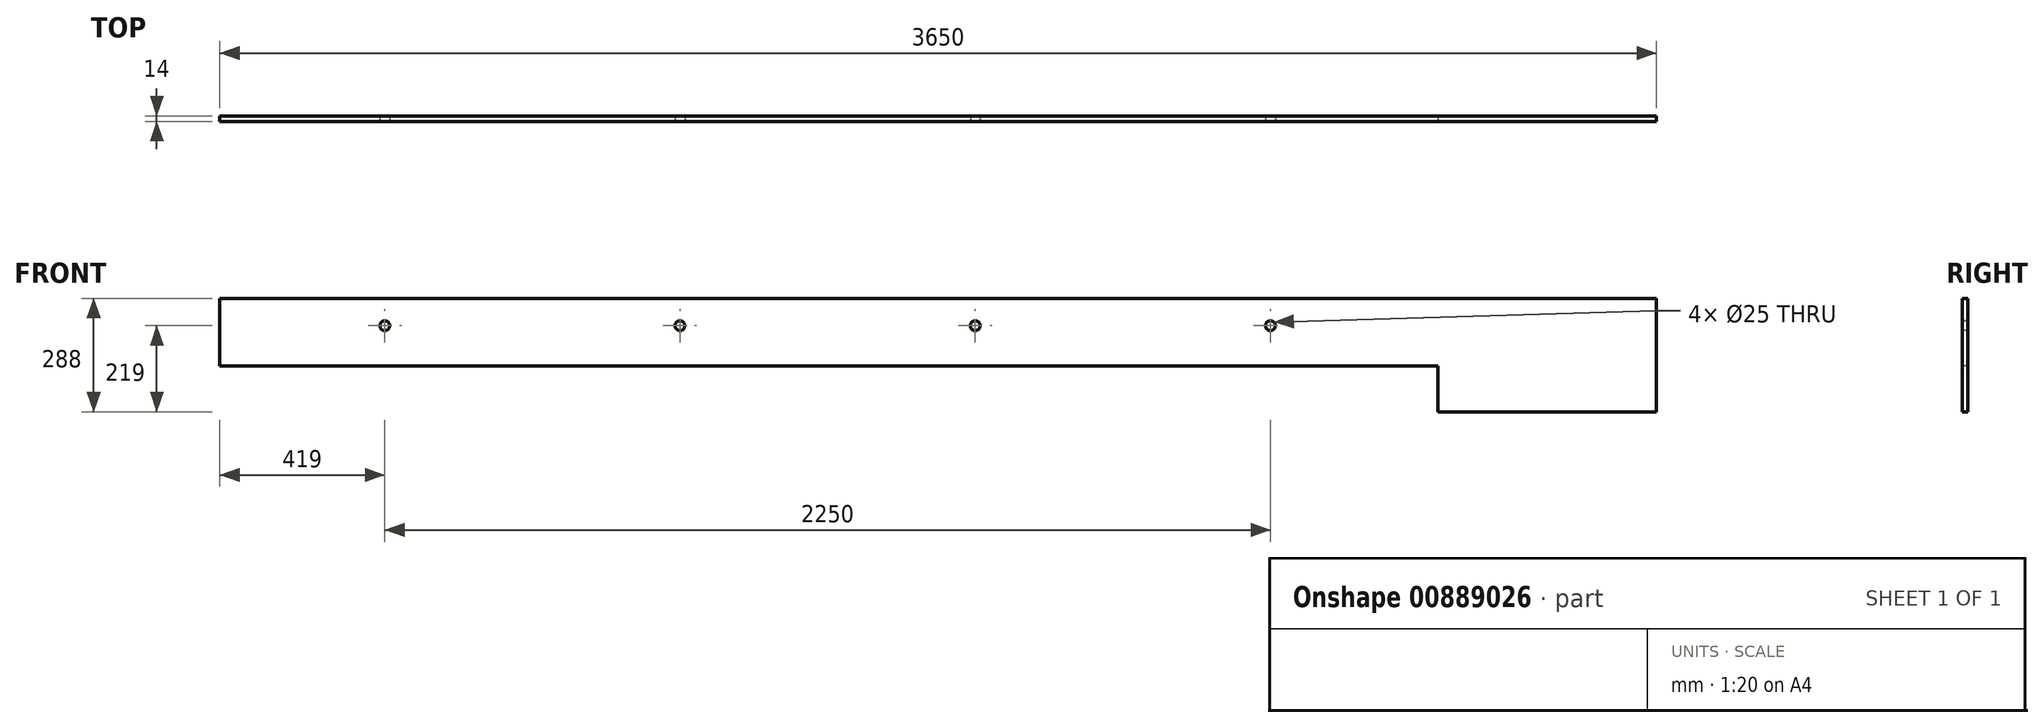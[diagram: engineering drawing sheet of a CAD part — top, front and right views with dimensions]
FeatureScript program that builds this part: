
annotation { "Feature Type Name" : "Feature", "Feature Type Description" : "" }
export const myFeature = defineFeature(function(context is Context, id is Id, definition is map)
    precondition{}
    {
        {
            var Q0;
            Q0=qCreatedBy(makeId("Right.planeOp"),FACE);
            var sketch = newSketch(context, id + "F0", { "sketchPlane" : qUnion([Q0])});
            skLineSegment(sketch, "E0.bottom", {"start": v(-7, 144) * mm, "end": v(7, 144) * mm});
            skLineSegment(sketch, "E0.top", {"start": v(-7, -144) * mm, "end": v(7, -144) * mm});
            skLineSegment(sketch, "E0.left", {"start": v(-7, 144) * mm, "end": v(-7, -144) * mm});
            skLineSegment(sketch, "E0.right", {"start": v(7, 144) * mm, "end": v(7, -144) * mm});
            skPoint(sketch, "E0.middle", {"position": v(0, 0) * mm});
            skSolve(sketch);
        }
        {
            var Q0;
            Q0 = qSketchRegion(id + "F0", true);
            extrude(context, id + "F1", {"entities" : qUnion([Q0]), "endBound" : BoundingType.SYMMETRIC, "depth" : 3650 * mm, "offsetDistance" : 25 * mm});
        }
        {
            var Q0;
            Q0=makeQuery(id+"F1.opExtrude","SWEPT_FACE",FACE,{"disambiguationData":[OSD([sQuery(id+"F0.wireOp",EDGE,"E0.left")])]});
            var sketch = newSketch(context, id + "F2", { "sketchPlane" : qUnion([Q0])});
            skLineSegment(sketch, "E1.bottom", {"start": v(-1825, -144) * mm, "end": v(1270, -144) * mm});
            skLineSegment(sketch, "E1.top", {"start": v(-1825, -27) * mm, "end": v(1270, -27) * mm});
            skLineSegment(sketch, "E1.left", {"start": v(-1825, -144) * mm, "end": v(-1825, -27) * mm});
            skLineSegment(sketch, "E1.right", {"start": v(1270, -144) * mm, "end": v(1270, -27) * mm});
            skSolve(sketch);
        }
        {
            var Q0;
            Q0 = qSketchRegion(id + "F2", true);
            extrude(context, id + "F3", {"entities" : qUnion([Q0]), "operationType" : NewBodyOperationType.REMOVE, "oppositeDirection" : true, "depth" : 25 * mm, "offsetDistance" : 25 * mm});
        }
        {
            var Q0;
            Q0=makeQuery(id+"F1.opExtrude","SWEPT_FACE",FACE,{"disambiguationData":[OSD([sQuery(id+"F0.wireOp",EDGE,"E0.left")])]});
            var sketch = newSketch(context, id + "F4", { "sketchPlane" : qUnion([Q0])});
            skCircle(sketch, "E2", {"center": v(-1406, 75) * mm, "radius": 12.5 * mm});
            skCircle(sketch, "E3.1.0.0", {"center": v(-656, 75) * mm, "radius": 12.5 * mm});
            skCircle(sketch, "E3.2.0.0", {"center": v(94, 75) * mm, "radius": 12.5 * mm});
            skCircle(sketch, "E3.3.0.0", {"center": v(844, 75) * mm, "radius": 12.5 * mm});
            skLineSegment(sketch, "E3.direction1", {"start": v(-1406, 75) * mm, "end": v(-656, 75) * mm, "construction": true});
            skSolve(sketch);
        }
        {
            var Q0;
            Q0 = qSketchRegion(id + "F4", true);
            extrude(context, id + "F5", {"entities" : qUnion([Q0]), "operationType" : NewBodyOperationType.REMOVE, "oppositeDirection" : true, "depth" : 25 * mm, "offsetDistance" : 25 * mm});
        }
    });
